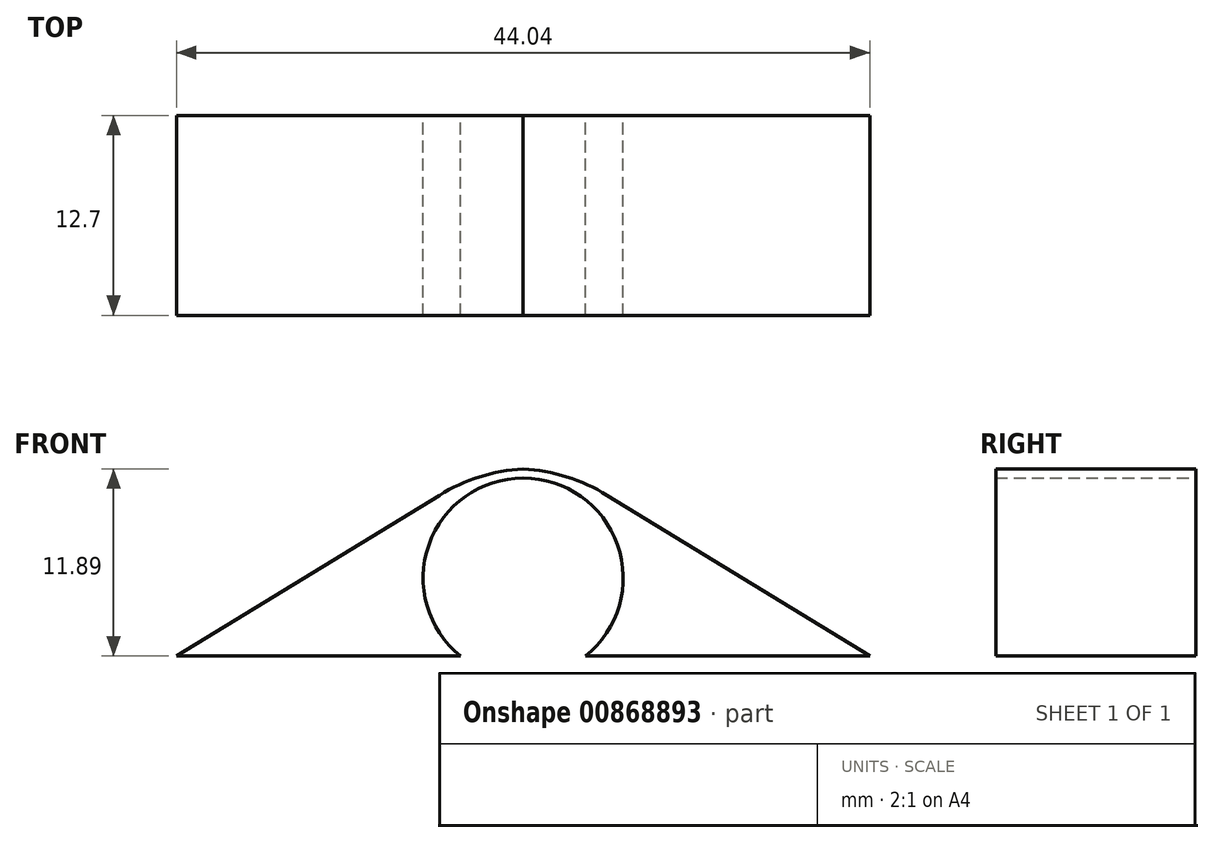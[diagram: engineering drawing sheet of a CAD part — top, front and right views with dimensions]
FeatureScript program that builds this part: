
annotation { "Feature Type Name" : "Feature", "Feature Type Description" : "" }
export const myFeature = defineFeature(function(context is Context, id is Id, definition is map)
    precondition{}
    {
        {
            var Q0;
            Q0=qCreatedBy(makeId("Front.planeOp"),FACE);
            var sketch = newSketch(context, id + "F0", { "sketchPlane" : qUnion([Q0])});
            skLineSegment(sketch, "E0", {"start": v(0, 0) * mm, "end": v(-22.02, 0) * mm});
            skLineSegment(sketch, "E1", {"start": v(-22.02, 0) * mm, "end": v(-5.32, 10.22) * mm});
            skArc(sketch, "E2", {"start": v(0, 11.89) * mm, "mid": v(-2.77, 11.38) * mm, "end": v(-5.32, 10.22) * mm});
            skArc(sketch, "E3.MirrorCS", {"start": v(0, 11.89) * mm, "mid": v(2.77, 11.38) * mm, "end": v(5.32, 10.22) * mm});
            skLineSegment(sketch, "E4.MirrorCS", {"start": v(22.02, 0) * mm, "end": v(5.32, 10.22) * mm});
            skLineSegment(sketch, "E5.MirrorCS", {"start": v(0, 0) * mm, "end": v(22.02, 0) * mm});
            skPoint(sketch, "E6", {"position": v(0, 4.96) * mm});
            skSolve(sketch);
        }
        {
            var Q0;
            Q0 = qSketchRegion(id + "F0", true);
            extrude(context, id + "F1", {"entities" : qUnion([Q0]), "depth" : 12.7 * mm, "offsetDistance" : 25.4 * mm});
        }
        {
            var Q0;
            Q0=sQuery(id+"F0.wireOp",VERTEX,"E6");
            var Q1;
            Q1=makeQuery(id+"F1.opExtrude","SWEPT_BODY",BODY,{"disambiguationData":[OSD([sQuery(id+"F0.wireOp",EDGE,"E0"),sQuery(id+"F0.wireOp",EDGE,"E1"),sQuery(id+"F0.wireOp",EDGE,"E2"),sQuery(id+"F0.wireOp",EDGE,"E3.MirrorCS"),sQuery(id+"F0.wireOp",EDGE,"E4.MirrorCS"),sQuery(id+"F0.wireOp",EDGE,"E5.MirrorCS")])]});
            hole(context, id + "F2", {"style" : HoleStyle.SIMPLE, "endStyle" : HoleEndStyle.THROUGH, "oppositeDirection" : true, "holeDiameter" : 12.7 * mm, "majorDiameter" : 6.35 * mm, "isTappedThrough" : true, "tappedDepth" : 12.7 * mm, "tapClearance" : 3, "locations" : qUnion([Q0]), "scope" : qUnion([Q1])});
        }
    });
